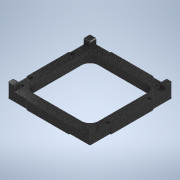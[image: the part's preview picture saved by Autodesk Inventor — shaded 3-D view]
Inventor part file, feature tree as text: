
AUTODESK INVENTOR PART (.ipt)
format: ipt  version: 2022 (Build 260153000, 153)  size: 316,416 bytes
history: native  units: mm
features: extrude x6, sketch x6, projected_geometry x4, fillet x2, chamfer x1
ambient origin geometry x8: Origin, YZ Plane, XZ Plane, XY Plane, X Axis, Y Axis, Z Axis, Center Point
bodies: Solid1 (feature_tree)
feature tree (19):
  extrude  "Extrusion1"  Depth=73.66mm
  extrude  "Extrusion2"  Depth=2.54mm
  extrude  "Extrusion3"  Depth=100.0mm
  fillet  "Fillet1"  Radius=100.0mm
  extrude  "Extrusion4"  Depth=10.0mm TaperAngle=0.0deg
  chamfer  "Chamfer1"  Distance=4.5mm
  extrude  "Extrusion5"  Depth=6.5mm
  fillet  "Fillet2"  Radius=6.2mm
  extrude  "Extrusion6"  Depth=1.2mm
  sketch  "Sketch1"  dims[d0=73.66mm d1=80.01mm]
  sketch  "Sketch4"  dims[d2=85.730001mm d3=2.54mm]
  projected_geometry  "Projected Loop2"
  sketch  "Sketch5"  dims[d4=3.81mm d6=2.9mm d7=100.0mm]
  projected_geometry  "Projected Loop3"
  sketch  "Sketch6"  dims[d8=100.0mm d10=10.0mm d11=0.0mm]
  projected_geometry  "Projected Loop4"
  sketch  "Sketch7"  dims[d13=4.5mm]
  projected_geometry  "Projected Loop5"
  sketch  "Sketch8"  dims[d14=4.5mm d15=4.5mm d16=4.5mm d17=6.2mm d18=0.0mm d19=1.2mm d20=1.2mm d21=25.0mm d22=25.0mm d23=0.0mm d24=0.0mm d25=40.0mm d27=360.0deg d29=1.0mm d30=7.3mm d31=7.3mm d32=6.5mm d33=0.0mm d34=1.0mm d35=2.0mm d36=45.0deg d37=40.0mm d39=360.0deg d50=11.0mm d51=11.0mm d52=11.0mm d53=11.0mm d54=10.0mm d55=0.0mm d56=10.0mm d57=91.6mm d58=49.4mm d59=4.2mm d60=4.2mm d61=4.2mm d62=4.2mm d63=6.5mm d64=0.0mm]
